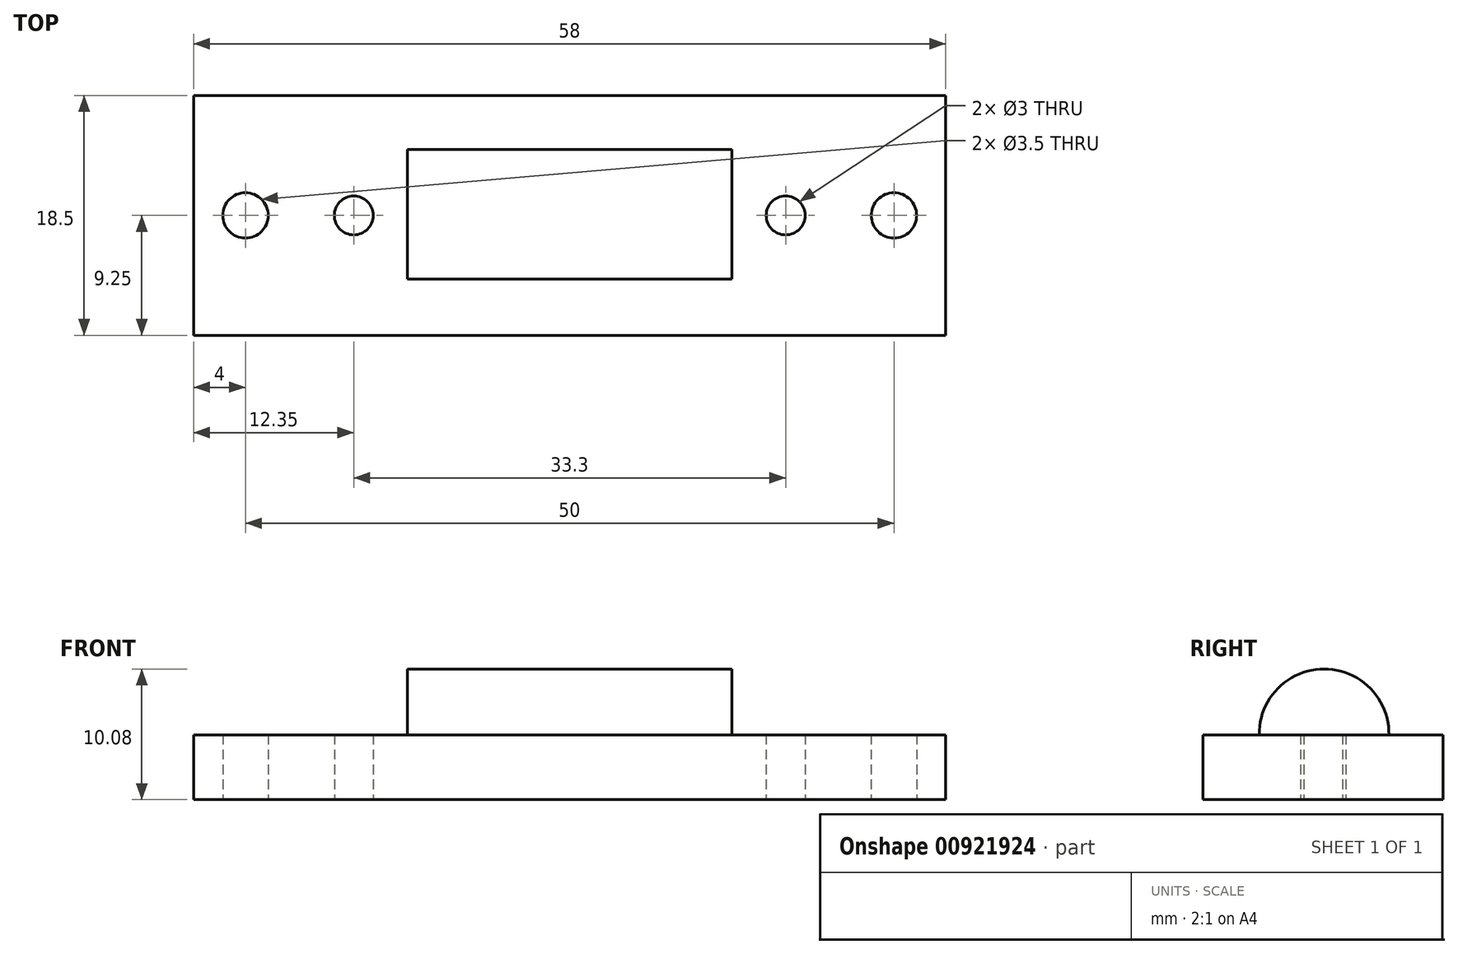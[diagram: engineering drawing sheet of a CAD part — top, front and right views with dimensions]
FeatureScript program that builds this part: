
annotation { "Feature Type Name" : "Feature", "Feature Type Description" : "" }
export const myFeature = defineFeature(function(context is Context, id is Id, definition is map)
    precondition{}
    {
        {
            var Q0;
            Q0=qCreatedBy(makeId("Top.planeOp"),FACE);
            var sketch = newSketch(context, id + "F0", { "sketchPlane" : qUnion([Q0])});
            skLineSegment(sketch, "E0.bottom", {"start": v(19, -9.25) * mm, "end": v(-19, -9.25) * mm});
            skLineSegment(sketch, "E0.top", {"start": v(19, 9.25) * mm, "end": v(-19, 9.25) * mm});
            skLineSegment(sketch, "E0.left", {"start": v(19, -9.25) * mm, "end": v(19, 9.25) * mm});
            skLineSegment(sketch, "E0.right", {"start": v(-19, -9.25) * mm, "end": v(-19, 9.25) * mm});
            skPoint(sketch, "E0.middle", {"position": v(0, 0) * mm});
            skLineSegment(sketch, "E1.bottom", {"start": v(19, -9.25) * mm, "end": v(29, -9.25) * mm});
            skLineSegment(sketch, "E1.top", {"start": v(19, 9.25) * mm, "end": v(29, 9.25) * mm});
            skLineSegment(sketch, "E1.right", {"start": v(29, -9.25) * mm, "end": v(29, 9.25) * mm});
            skLineSegment(sketch, "E2.bottom", {"start": v(-19, -9.25) * mm, "end": v(-29, -9.25) * mm});
            skLineSegment(sketch, "E2.top", {"start": v(-19, 9.25) * mm, "end": v(-29, 9.25) * mm});
            skLineSegment(sketch, "E2.right", {"start": v(-29, -9.25) * mm, "end": v(-29, 9.25) * mm});
            skCircle(sketch, "E3", {"center": v(-25, 0) * mm, "radius": 1.75 * mm});
            skPoint(sketch, "E3.centerSnap0", {"position": v(-29, 0) * mm});
            skCircle(sketch, "E4", {"center": v(25, 0) * mm, "radius": 1.75 * mm});
            skPoint(sketch, "E4.centerSnap0", {"position": v(29, 0) * mm});
            skCircle(sketch, "E5", {"center": v(-16.65, 0) * mm, "radius": 1.5 * mm});
            skCircle(sketch, "E6", {"center": v(16.65, 0) * mm, "radius": 1.5 * mm});
            skSolve(sketch);
        }
        {
            var Q0;
            Q0=qSketchRegion(id+"F0",true);
            extrude(context, id + "F1", {"entities" : qUnion([Q0]), "depth" : 5 * mm, "offsetDistance" : 25 * mm});
        }
        {
            var Q0;
            Q0=makeQuery(id+"F1.opExtrude","CAP_FACE",FACE,{"disambiguationData":[OSD([sQuery(id+"F0.wireOp",EDGE,"E0.bottom"),sQuery(id+"F0.wireOp",EDGE,"E0.top"),sQuery(id+"F0.wireOp",EDGE,"E1.bottom"),sQuery(id+"F0.wireOp",EDGE,"E1.top"),sQuery(id+"F0.wireOp",EDGE,"E1.right"),sQuery(id+"F0.wireOp",EDGE,"E2.bottom"),sQuery(id+"F0.wireOp",EDGE,"E2.top"),sQuery(id+"F0.wireOp",EDGE,"E2.right"),sQuery(id+"F0.wireOp",EDGE,"E3"),sQuery(id+"F0.wireOp",EDGE,"E4"),sQuery(id+"F0.wireOp",EDGE,"E5"),sQuery(id+"F0.wireOp",EDGE,"E6")])],"isStart":false});
            var sketch = newSketch(context, id + "F2", { "sketchPlane" : qUnion([Q0])});
            skLineSegment(sketch, "E7.bottom", {"start": v(12.5, 9.25) * mm, "end": v(-12.5, 9.25) * mm});
            skLineSegment(sketch, "E7.top", {"start": v(12.5, -9.25) * mm, "end": v(-12.5, -9.25) * mm});
            skLineSegment(sketch, "E7.left", {"start": v(12.5, 9.25) * mm, "end": v(12.5, -9.25) * mm});
            skLineSegment(sketch, "E7.right", {"start": v(-12.5, 9.25) * mm, "end": v(-12.5, -9.25) * mm});
            skPoint(sketch, "E7.middle", {"position": v(0, 0) * mm});
            skSolve(sketch);
        }
        {
            var Q0;
            Q0=qSketchRegion(id+"F2",true);
            extrude(context, id + "F3", {"entities" : qUnion([Q0]), "operationType" : NewBodyOperationType.ADD, "depth" : (18.5 / 2) * mm, "offsetDistance" : 25 * mm});
        }
        {
            var Q0;
            Q0=makeQuery(id+"F3.opExtrude","SWEPT_FACE",FACE,{"disambiguationData":[OSD([sQuery(id+"F2.wireOp",EDGE,"E7.left")])]});
            var sketch = newSketch(context, id + "F4", { "sketchPlane" : qUnion([Q0])});
            skArc(sketch, "E8", {"start": v(5.08, 5) * mm, "mid": v(0.08, 10.08) * mm, "end": v(-4.92, 5) * mm});
            skLineSegment(sketch, "E9.bottom", {"start": v(-9.25, 14.25) * mm, "end": v(9.25, 14.25) * mm});
            skLineSegment(sketch, "E9.top", {"start": v(-9.25, 5) * mm, "end": v(9.25, 5) * mm});
            skLineSegment(sketch, "E9.left", {"start": v(-9.25, 14.25) * mm, "end": v(-9.25, 5) * mm});
            skLineSegment(sketch, "E9.right", {"start": v(9.25, 14.25) * mm, "end": v(9.25, 5) * mm});
            skSolve(sketch);
        }
        {
            var Q0;
            {var subQ2=sQuery(id+"F4.wireOp",EDGE,"E8");Q0=makeQuery(id+"F4.imprint","IMPRINT",FACE,{"disambiguationData":[TD([[makeQuery(id+"F4.imprint","IMPRINT",EDGE,{"derivedFrom":subQ2}),-1.0]])]});}
            extrude(context, id + "F5", {"entities" : qUnion([Q0]), "operationType" : NewBodyOperationType.REMOVE, "oppositeDirection" : true, "depth" : 25 * mm, "offsetDistance" : 25 * mm});
        }
    });
